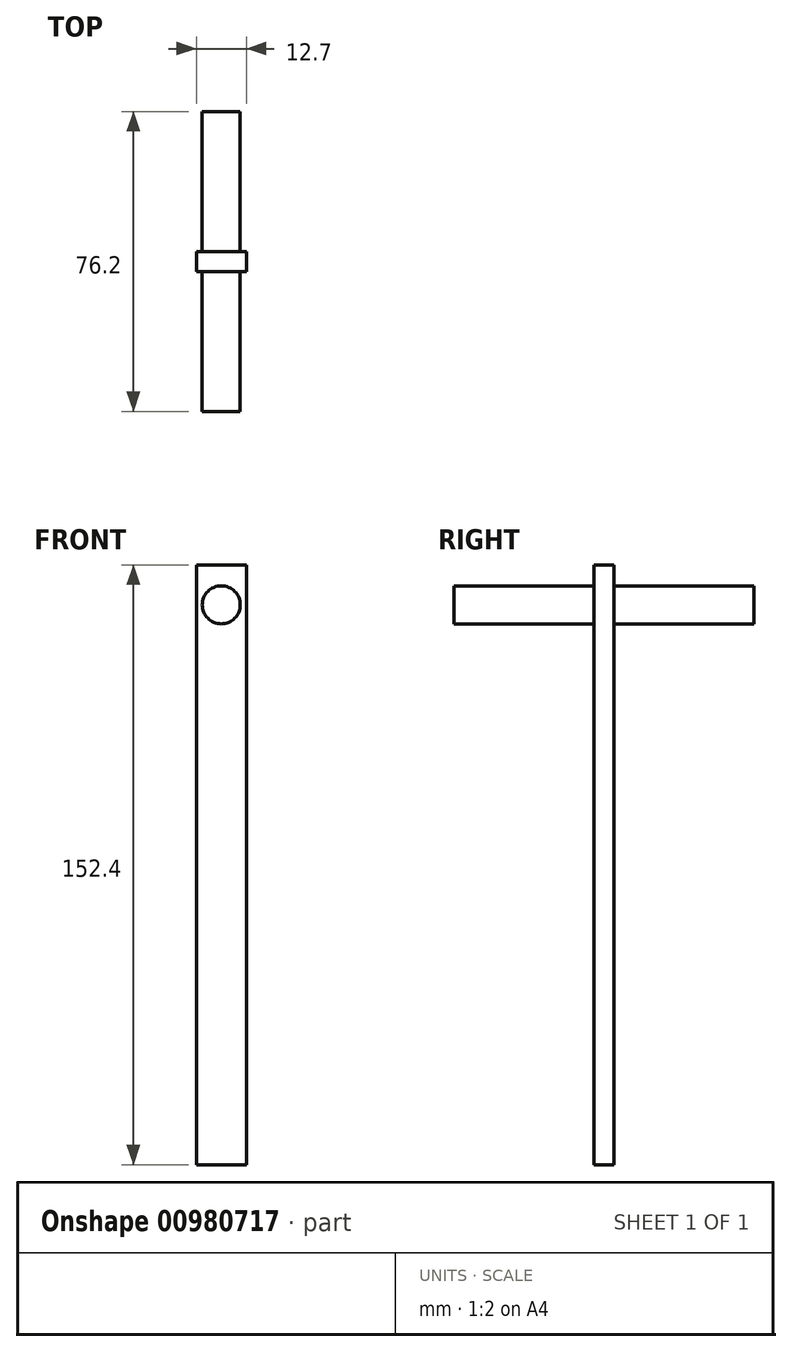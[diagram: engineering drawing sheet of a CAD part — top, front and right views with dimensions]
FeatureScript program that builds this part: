
annotation { "Feature Type Name" : "Feature", "Feature Type Description" : "" }
export const myFeature = defineFeature(function(context is Context, id is Id, definition is map)
    precondition{}
    {
        {
            var Q0;
            Q0=qCreatedBy(makeId("Top.planeOp"),FACE);
            var sketch = newSketch(context, id + "F0", { "sketchPlane" : qUnion([Q0])});
            skLineSegment(sketch, "E0.bottom", {"start": v(-6.35, 2.54) * mm, "end": v(6.35, 2.54) * mm});
            skLineSegment(sketch, "E0.top", {"start": v(-6.35, -2.54) * mm, "end": v(6.35, -2.54) * mm});
            skLineSegment(sketch, "E0.left", {"start": v(-6.35, 2.54) * mm, "end": v(-6.35, -2.54) * mm});
            skLineSegment(sketch, "E0.right", {"start": v(6.35, 2.54) * mm, "end": v(6.35, -2.54) * mm});
            skSolve(sketch);
        }
        {
            var Q0;
            Q0=makeQuery(id+"F0.imprint","IMPRINT",FACE,{"disambiguationData":[TD([[makeQuery(id+"F0.imprint","IMPRINT",EDGE,{"derivedFrom":sQuery(id+"F0.wireOp",EDGE,"E0.bottom")}),-1.0]])]});
            extrude(context, id + "F1", {"entities" : qUnion([Q0]), "endBound" : BoundingType.SYMMETRIC, "depth" : 152.4 * mm, "offsetDistance" : 25.4 * mm});
        }
        {
            var Q0;
            Q0=qCreatedBy(makeId("Front.planeOp"),FACE);
            var sketch = newSketch(context, id + "F2", { "sketchPlane" : qUnion([Q0])});
            skCircle(sketch, "E1", {"center": v(0, 66.04) * mm, "radius": 4.83 * mm});
            skLineSegment(sketch, "E2", {"start": v(0, 0) * mm, "end": v(0, 79.03) * mm, "construction": true});
            skSolve(sketch);
        }
        {
            var Q0;
            Q0 = qSketchRegion(id + "F2", true);
            var Q1;
            Q1=sQuery(id+"F2.wireOp",EDGE,"E1");
            extrude(context, id + "F3", {"entities" : qUnion([Q0]), "operationType" : NewBodyOperationType.ADD, "surfaceEntities" : qUnion([Q1]), "endBound" : BoundingType.SYMMETRIC, "depth" : 76.2 * mm, "offsetDistance" : 25.4 * mm});
        }
    });
